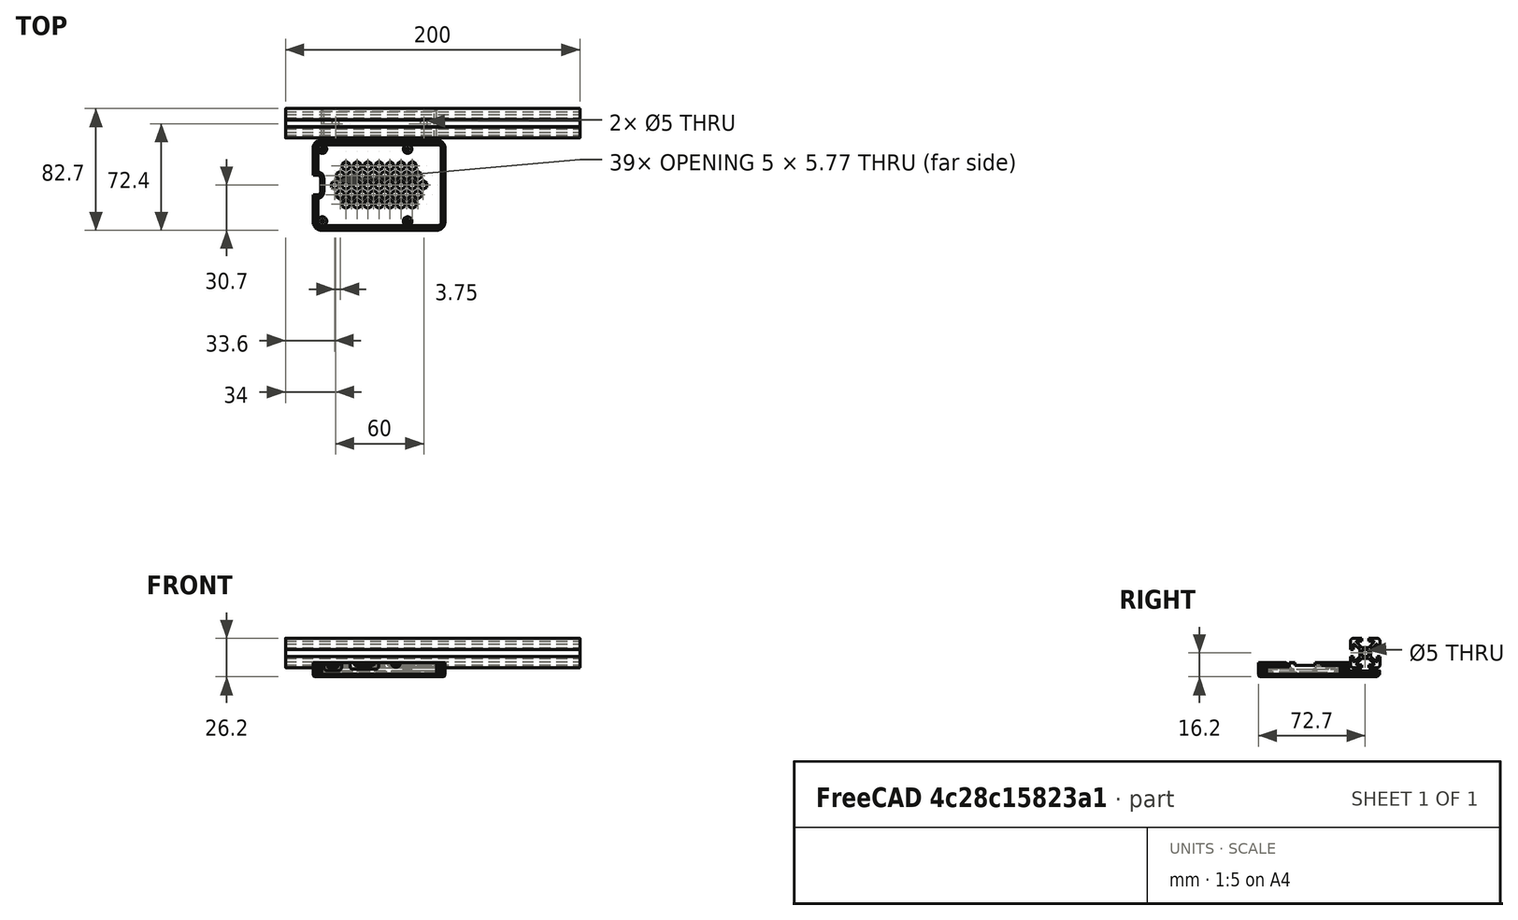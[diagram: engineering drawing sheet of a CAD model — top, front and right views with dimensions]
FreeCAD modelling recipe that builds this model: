
FCSTD DOCUMENT  (FreeCAD 1.1R44348 (Git))
Label: BaseRp32020
License: All rights reserved
LicenseURL: https://en.wikipedia.org/wiki/All_rights_reserved
objects: Part::Feature×3, Sketcher::SketchObject×2, Mesh::Feature×1, Part::Refine×1, App::Point×1, PartDesign::FeatureBase×1, PartDesign::Pad×1, PartDesign::Pocket×1, PartDesign::Chamfer×1, PartDesign::Fillet×1, PartDesign::Body×1
note: 23 computed .brp shape members not serialized (recipe doc carries the construction recipe); baked Part::Feature solids carry a one-line shape summary decoded from their .brp

FEATURE [Mesh::Feature] bottom_hex_sm
FEATURE [Part::Feature] bottom_hex_sm001
  shape: bbox 89.6 x 61.4 x 9.7 mm, 7850 faces, 0 solids (baked)
FEATURE [Part::Refine] bottom_hex_sm002
  Source = -> bottom_hex_sm001
FEATURE [Part::Feature] bottom_hex_sm002_solid  label="bottom_hex_sm002 (Solid)"
  shape: bbox 89.6 x 61.4 x 9.7 mm, 3412 faces (baked)
FEATURE [App::Point] Origin001
  Role = Origin
FEATURE [PartDesign::FeatureBase] BaseFeature
  BaseFeature = -> bottom_hex_sm002_solid
  Suppressed = false
FEATURE [Sketcher::SketchObject] Sketch
  ArcFitTolerance = 1e-06
  AttachmentOffset = pos=(0,0,-1) rot=(0,0,1;0rad)
  AttachmentSupport = -> [BaseFeature]
  ExternalGeometry = -> [BaseFeature]
  ExternalTypes = [0]
  FullyConstrained = true
  MakeInternals = false
  MapMode = 5
  Placement = pos=(0,57.7,2e-16) rot=(0,0.707107,0.707107;3.14159rad)
  sketch-geometry (4):
    g0: LineSegment StartX=-38.7 StartY=-5.2 StartZ=0 EndX=39.5 EndY=-5.2 EndZ=0
    g1: LineSegment StartX=39.5 StartY=-5.2 StartZ=0 EndX=39.5 EndY=-1.2 EndZ=0
    g2: LineSegment StartX=39.5 StartY=-1.2 StartZ=0 EndX=-38.7 EndY=-1.2 EndZ=0
    g3: LineSegment StartX=-38.7 StartY=-1.2 StartZ=0 EndX=-38.7 EndY=-5.2 EndZ=0
  constraints (10):
    c: Coincident(g0,g1)
    c: Coincident(g1,g2)
    c: Coincident(g2,g3)
    c: Coincident(g3,g0)
    c: Horizontal(g2)
    c: Vertical(g1)
    c: Vertical(g3)
    c: Coincident(g0,g-3)
    c: Coincident(g-3,g0)
    c: Distance(g1,g1) = 4
FEATURE [PartDesign::Pad] Pad
  BaseFeature = -> BaseFeature
  Direction = (0,1,0)
  Length = 22
  Length2 = 10
  Profile = -> Sketch
  ReferenceAxis = -> Sketch [N_Axis]
  Refine = true
  SideType = 0
  Suppressed = false
  Type = 0
  Type2 = 0
FEATURE [Sketcher::SketchObject] Sketch001
  ArcFitTolerance = 1e-06
  AttachmentSupport = -> [Pad]
  ExternalGeometry = -> [Pad]
  ExternalTypes = [0,0]
  FullyConstrained = true
  MakeInternals = false
  MapMode = 5
  Placement = pos=(0,-3e-16,-1.2) rot=(0,0,1;0rad)
  sketch-geometry (2):
    g0: Circle CenterX=-30 CenterY=69.7 CenterZ=0 NormalX=0 NormalY=0 NormalZ=1 AngleXU=0 Radius=2.5
    g1: Circle CenterX=30 CenterY=69.7 CenterZ=0 NormalX=0 NormalY=0 NormalZ=1 AngleXU=0 Radius=2.5
  constraints (5):
    c: Equal(g0,g1)
    c: Diameter(g0) = 5
    c: Symmetric(g0,g1,g-2)
    c: DistanceY(g0,g-3) = 10
    c: DistanceX(g0,g1) = 60
FEATURE [PartDesign::Pocket] Pocket
  BaseFeature = -> Pad
  Direction = (0,0,-1)
  Length = 5
  Length2 = 5
  Profile = -> Sketch001
  ReferenceAxis = -> Sketch001 [N_Axis]
  Refine = true
  SideType = 0
  Suppressed = false
  Type = 0
  Type2 = 0
FEATURE [Part::Feature] Part__Feature  label="profil_alu_parametryzowany v1"
  Placement = pos=(-64,70,11) rot=(0,1,0;1.5708rad)
  shape: bbox 200 x 20.01 x 20.01 mm, 51 faces (baked)
FEATURE [PartDesign::Chamfer] Chamfer
  Angle = 45
  Base = -> Pocket [Edge80,Edge78,Edge76]
  BaseFeature = -> Pocket
  ChamferType = 0
  FlipDirection = false
  Refine = true
  Size = 1.7
  Size2 = 1
  SupportTransform = false
  Suppressed = false
  UseAllEdges = false
FEATURE [PartDesign::Fillet] Fillet
  Base = -> Chamfer [Edge1106,Edge1114]
  BaseFeature = -> Chamfer
  Radius = 1
  Refine = true
  SupportTransform = false
  Suppressed = false
  UseAllEdges = false
FEATURE [PartDesign::Body] Body
  AllowCompound = true
  BaseFeature = -> bottom_hex_sm002_solid
  Group = -> [BaseFeature,Sketch,Pad,Sketch001,Pocket,Chamfer,Fillet]
  Origin = -> Origin
  Tip = -> Fillet
